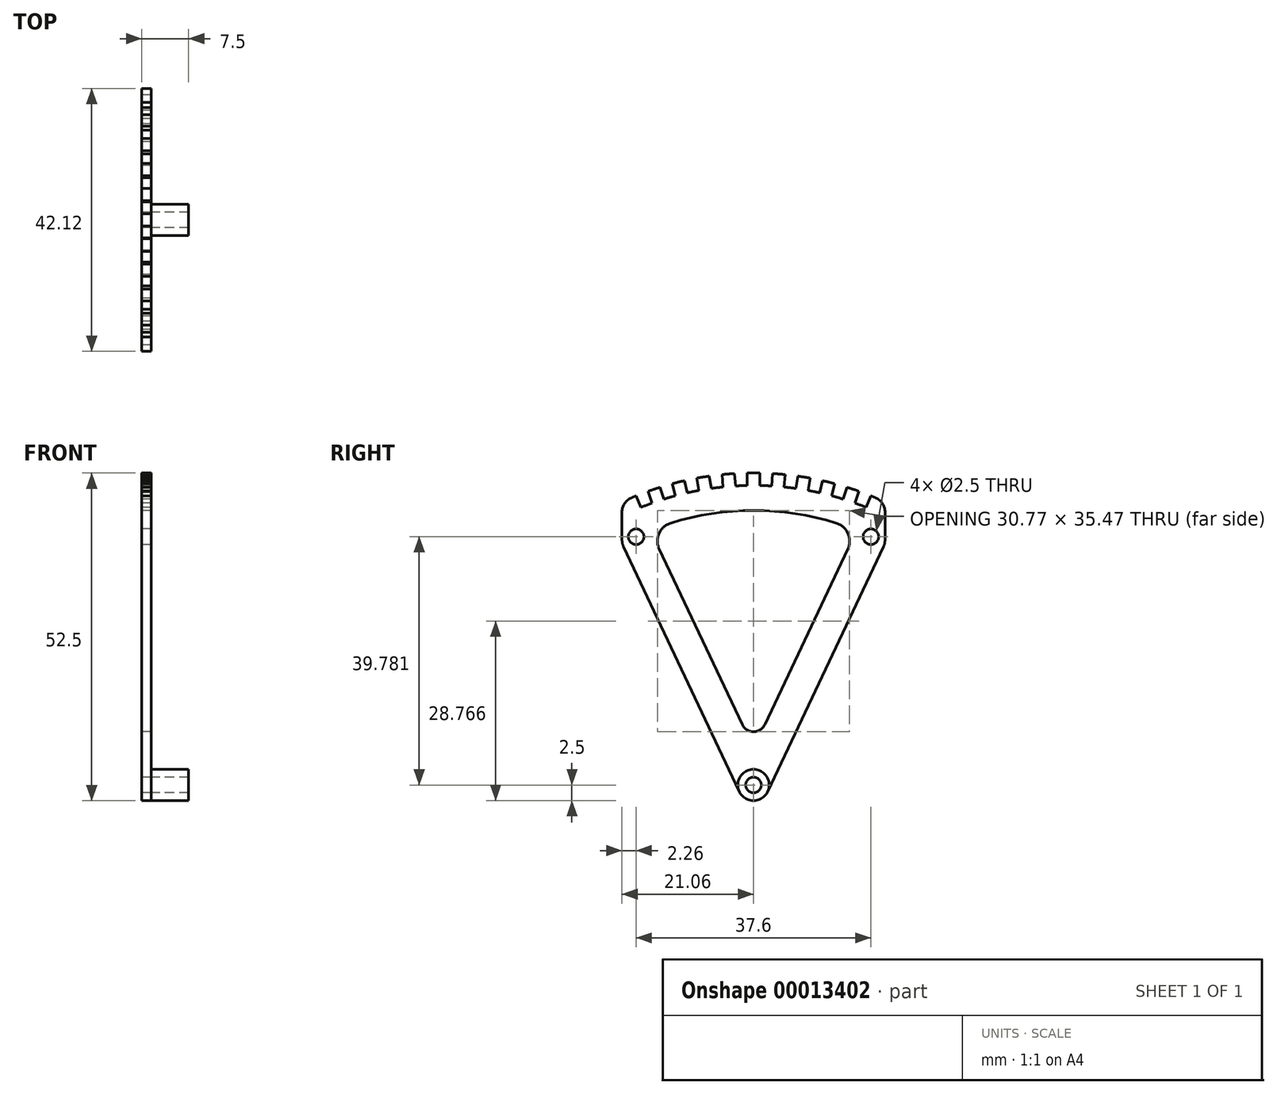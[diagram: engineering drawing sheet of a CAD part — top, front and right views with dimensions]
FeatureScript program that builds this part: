
annotation { "Feature Type Name" : "Feature", "Feature Type Description" : "" }
export const myFeature = defineFeature(function(context is Context, id is Id, definition is map)
    precondition{}
    {
        {
            var Q0;
            Q0=qCreatedBy(makeId("Right.planeOp"),FACE);
            var sketch = newSketch(context, id + "F0", { "sketchPlane" : qUnion([Q0])});
            skCircle(sketch, "E0", {"center": v(0, 0) * mm, "radius": 44 * mm});
            skCircle(sketch, "E1", {"center": v(0, 0) * mm, "radius": 48 * mm});
            skCircle(sketch, "E2", {"center": v(0, 0) * mm, "radius": 50 * mm});
            skLineSegment(sketch, "E3", {"start": v(0, 0) * mm, "end": v(0, 50) * mm, "construction": true});
            skLineSegment(sketch, "E4", {"start": v(-18.8, 39.78) * mm, "end": v(18.8, 39.78) * mm, "construction": true});
            skLineSegment(sketch, "E5", {"start": v(0, 0) * mm, "end": v(-18.8, 39.78) * mm, "construction": true});
            skLineSegment(sketch, "E6.0", {"start": v(2.26, 1.07) * mm, "end": v(-16.54, 40.85) * mm});
            skLineSegment(sketch, "E7.0.MirrorCS", {"start": v(-2.26, -1.07) * mm, "end": v(-21.06, 38.71) * mm});
            skLineSegment(sketch, "E8", {"start": v(-21.06, 38.71) * mm, "end": v(-21.06, 45.35) * mm});
            skPoint(sketch, "E9.orphan", {"position": v(-2.26, -1.07) * mm});
            skLineSegment(sketch, "E10.rect.bottom", {"start": v(-1, 50.26) * mm, "end": v(1, 50.26) * mm});
            skLineSegment(sketch, "E10.rect.top", {"start": v(-1, 45.74) * mm, "end": v(1, 45.74) * mm});
            skLineSegment(sketch, "E10.rect.left", {"start": v(-1, 50.26) * mm, "end": v(-1, 45.74) * mm});
            skLineSegment(sketch, "E10.rect.right", {"start": v(1, 50.26) * mm, "end": v(1, 45.74) * mm});
            skPoint(sketch, "E10.rect.middle", {"position": v(0, 48) * mm});
            skLineSegment(sketch, "E11.1.0", {"start": v(-3.07, 50.18) * mm, "end": v(-2.7, 45.67) * mm});
            skLineSegment(sketch, "E11.1.1", {"start": v(-5.07, 50.01) * mm, "end": v(-4.7, 45.5) * mm});
            skLineSegment(sketch, "E11.1.2", {"start": v(-5.07, 50.01) * mm, "end": v(-3.07, 50.18) * mm});
            skLineSegment(sketch, "E11.2.0", {"start": v(-7.13, 49.76) * mm, "end": v(-6.4, 45.3) * mm});
            skLineSegment(sketch, "E11.2.1", {"start": v(-9.1, 49.44) * mm, "end": v(-8.37, 44.98) * mm});
            skLineSegment(sketch, "E11.2.2", {"start": v(-9.1, 49.44) * mm, "end": v(-7.13, 49.76) * mm});
            skLineSegment(sketch, "E11.3.0", {"start": v(-11.14, 49.02) * mm, "end": v(-10.05, 44.63) * mm});
            skLineSegment(sketch, "E11.3.1", {"start": v(-13.08, 48.54) * mm, "end": v(-11.99, 44.15) * mm});
            skLineSegment(sketch, "E11.3.2", {"start": v(-13.08, 48.54) * mm, "end": v(-11.14, 49.02) * mm});
            skLineSegment(sketch, "E11.4.0", {"start": v(-15.07, 47.96) * mm, "end": v(-13.63, 43.67) * mm});
            skLineSegment(sketch, "E11.4.1", {"start": v(-16.97, 47.32) * mm, "end": v(-15.53, 43.03) * mm});
            skLineSegment(sketch, "E11.4.2", {"start": v(-16.97, 47.32) * mm, "end": v(-15.07, 47.96) * mm});
            skLineSegment(sketch, "E11.5.0", {"start": v(-18.9, 46.58) * mm, "end": v(-17.12, 42.42) * mm});
            skLineSegment(sketch, "E11.5.1", {"start": v(-20.75, 45.8) * mm, "end": v(-18.96, 41.64) * mm});
            skLineSegment(sketch, "E11.5.2", {"start": v(-20.75, 45.8) * mm, "end": v(-18.9, 46.58) * mm});
            skLineSegment(sketch, "E11.anchor1", {"start": v(0, 0) * mm, "end": v(1, 45.74) * mm, "construction": true});
            skLineSegment(sketch, "E11.anchor2", {"start": v(0, 0) * mm, "end": v(-17.12, 42.42) * mm, "construction": true});
            skLineSegment(sketch, "E12.0.MirrorCS", {"start": v(-2.26, 1.07) * mm, "end": v(16.54, 40.85) * mm});
            skLineSegment(sketch, "E13.0.MirrorCS", {"start": v(2.26, -1.07) * mm, "end": v(21.06, 38.71) * mm});
            skLineSegment(sketch, "E14.0.MirrorCS", {"start": v(21.06, 38.71) * mm, "end": v(21.06, 45.35) * mm});
            skLineSegment(sketch, "E15.0.MirrorCS", {"start": v(18.9, 46.58) * mm, "end": v(17.12, 42.42) * mm});
            skLineSegment(sketch, "E16.0.MirrorCS", {"start": v(16.97, 47.32) * mm, "end": v(15.53, 43.03) * mm});
            skLineSegment(sketch, "E17.0.MirrorCS", {"start": v(15.07, 47.96) * mm, "end": v(13.63, 43.67) * mm});
            skLineSegment(sketch, "E18.0.MirrorCS", {"start": v(13.08, 48.54) * mm, "end": v(11.99, 44.15) * mm});
            skLineSegment(sketch, "E19.0.MirrorCS", {"start": v(11.14, 49.02) * mm, "end": v(10.05, 44.63) * mm});
            skLineSegment(sketch, "E20.0.MirrorCS", {"start": v(9.1, 49.44) * mm, "end": v(8.37, 44.98) * mm});
            skLineSegment(sketch, "E21.0.MirrorCS", {"start": v(7.13, 49.76) * mm, "end": v(6.4, 45.3) * mm});
            skLineSegment(sketch, "E22.0.MirrorCS", {"start": v(5.07, 50.01) * mm, "end": v(4.7, 45.5) * mm});
            skLineSegment(sketch, "E23.0.MirrorCS", {"start": v(3.07, 50.18) * mm, "end": v(2.7, 45.67) * mm});
            skCircle(sketch, "E24", {"center": v(-18.8, 39.78) * mm, "radius": 1.25 * mm});
            skCircle(sketch, "E25", {"center": v(0, 0) * mm, "radius": 1.25 * mm});
            skCircle(sketch, "E26.0.MirrorC", {"center": v(18.8, 39.78) * mm, "radius": 1.25 * mm});
            skPoint(sketch, "E27.visualSharp", {"position": v(0, -5.85) * mm});
            skArc(sketch, "E27.filletArc", {"start": v(-2.26, -1.07) * mm, "mid": v(0, -2.5) * mm, "end": v(2.26, -1.07) * mm});
            skSolve(sketch);
        }
        {
            var Q0;
            Q0=makeQuery(id+"F0.imprint","IMPRINT",FACE,{"disambiguationData":[TD([[makeQuery(id+"F0.imprint","IMPRINT",EDGE,{"derivedFrom":sQuery(id+"F0.wireOp",EDGE,"E25")}),-1.0]])]});
            var Q1;
            {var subQ63=sQuery(id+"F0.wireOp",EDGE,"E10.rect.top");Q1=makeQuery(id+"F0.imprint","IMPRINT",FACE,{"disambiguationData":[TD([[makeQuery(id+"F0.imprint","IMPRINT",EDGE,{"derivedFrom":subQ63}),-1.0]])]});}
            var Q2;
            {var subQ3=sQuery(id+"F0.wireOp",EDGE,"E10.rect.top");Q2=makeQuery(id+"F0.imprint","IMPRINT",FACE,{"disambiguationData":[TD([[makeQuery(id+"F0.imprint","IMPRINT",EDGE,{"derivedFrom":subQ3}),1.0]])]});}
            var Q3;
            {var subQ0=sQuery(id+"F0.wireOp",EDGE,"E11.5.1");var subQ3=sQuery(id+"F0.wireOp",EDGE,"E1");var subQ4=makeQuery(id+"F0.imprint","INTERSECT",VERTEX,{"derivedFrom":[subQ3,subQ0]});Q3=makeQuery(id+"F0.imprint","IMPRINT",FACE,{"disambiguationData":[TD([[makeQuery(id+"F0.imprint","IMPRINT",EDGE,{"disambiguationData":[TD([[subQ4,-1.0]])],"derivedFrom":subQ3}),-1.0]])]});}
            var Q4;
            {var subQ3=sQuery(id+"F0.wireOp",EDGE,"E11.5.0");var subQ5=sQuery(id+"F0.wireOp",EDGE,"E1");var subQ7=makeQuery(id+"F0.imprint","INTERSECT",VERTEX,{"derivedFrom":[subQ5,subQ3]});Q4=makeQuery(id+"F0.imprint","IMPRINT",FACE,{"disambiguationData":[TD([[makeQuery(id+"F0.imprint","IMPRINT",EDGE,{"disambiguationData":[TD([[subQ7,-1.0]])],"derivedFrom":subQ5}),-1.0]])]});}
            var Q5;
            {var subQ3=sQuery(id+"F0.wireOp",EDGE,"E11.4.0");var subQ5=sQuery(id+"F0.wireOp",EDGE,"E1");var subQ7=makeQuery(id+"F0.imprint","INTERSECT",VERTEX,{"derivedFrom":[subQ5,subQ3]});Q5=makeQuery(id+"F0.imprint","IMPRINT",FACE,{"disambiguationData":[TD([[makeQuery(id+"F0.imprint","IMPRINT",EDGE,{"disambiguationData":[TD([[subQ7,-1.0]])],"derivedFrom":subQ5}),-1.0]])]});}
            var Q6;
            {var subQ3=sQuery(id+"F0.wireOp",EDGE,"E11.3.0");var subQ5=sQuery(id+"F0.wireOp",EDGE,"E1");var subQ7=makeQuery(id+"F0.imprint","INTERSECT",VERTEX,{"derivedFrom":[subQ5,subQ3]});Q6=makeQuery(id+"F0.imprint","IMPRINT",FACE,{"disambiguationData":[TD([[makeQuery(id+"F0.imprint","IMPRINT",EDGE,{"disambiguationData":[TD([[subQ7,-1.0]])],"derivedFrom":subQ5}),-1.0]])]});}
            var Q7;
            {var subQ3=sQuery(id+"F0.wireOp",EDGE,"E11.2.0");var subQ5=sQuery(id+"F0.wireOp",EDGE,"E1");var subQ7=makeQuery(id+"F0.imprint","INTERSECT",VERTEX,{"derivedFrom":[subQ5,subQ3]});Q7=makeQuery(id+"F0.imprint","IMPRINT",FACE,{"disambiguationData":[TD([[makeQuery(id+"F0.imprint","IMPRINT",EDGE,{"disambiguationData":[TD([[subQ7,-1.0]])],"derivedFrom":subQ5}),-1.0]])]});}
            var Q8;
            {var subQ3=sQuery(id+"F0.wireOp",EDGE,"E11.1.0");var subQ5=sQuery(id+"F0.wireOp",EDGE,"E1");var subQ7=makeQuery(id+"F0.imprint","INTERSECT",VERTEX,{"derivedFrom":[subQ5,subQ3]});Q8=makeQuery(id+"F0.imprint","IMPRINT",FACE,{"disambiguationData":[TD([[makeQuery(id+"F0.imprint","IMPRINT",EDGE,{"disambiguationData":[TD([[subQ7,-1.0]])],"derivedFrom":subQ5}),-1.0]])]});}
            var Q9;
            {var subQ1=sQuery(id+"F0.wireOp",EDGE,"E10.rect.right");var subQ5=sQuery(id+"F0.wireOp",EDGE,"E1");var subQ6=makeQuery(id+"F0.imprint","INTERSECT",VERTEX,{"derivedFrom":[subQ5,subQ1]});Q9=makeQuery(id+"F0.imprint","IMPRINT",FACE,{"disambiguationData":[TD([[makeQuery(id+"F0.imprint","IMPRINT",EDGE,{"disambiguationData":[TD([[subQ6,-1.0]])],"derivedFrom":subQ5}),-1.0]])]});}
            var Q10;
            {var subQ1=sQuery(id+"F0.wireOp",EDGE,"E1");var subQ5=sQuery(id+"F0.wireOp",EDGE,"E22.0.MirrorCS");var subQ6=makeQuery(id+"F0.imprint","INTERSECT",VERTEX,{"derivedFrom":[subQ1,subQ5]});Q10=makeQuery(id+"F0.imprint","IMPRINT",FACE,{"disambiguationData":[TD([[makeQuery(id+"F0.imprint","IMPRINT",EDGE,{"disambiguationData":[TD([[subQ6,-1.0]])],"derivedFrom":subQ1}),-1.0]])]});}
            var Q11;
            {var subQ1=sQuery(id+"F0.wireOp",EDGE,"E1");var subQ5=sQuery(id+"F0.wireOp",EDGE,"E20.0.MirrorCS");var subQ7=makeQuery(id+"F0.imprint","INTERSECT",VERTEX,{"derivedFrom":[subQ1,subQ5]});Q11=makeQuery(id+"F0.imprint","IMPRINT",FACE,{"disambiguationData":[TD([[makeQuery(id+"F0.imprint","IMPRINT",EDGE,{"disambiguationData":[TD([[subQ7,-1.0]])],"derivedFrom":subQ1}),-1.0]])]});}
            var Q12;
            {var subQ0=sQuery(id+"F0.wireOp",EDGE,"E18.0.MirrorCS");var subQ1=sQuery(id+"F0.wireOp",EDGE,"E1");var subQ2=makeQuery(id+"F0.imprint","INTERSECT",VERTEX,{"derivedFrom":[subQ1,subQ0]});Q12=makeQuery(id+"F0.imprint","IMPRINT",FACE,{"disambiguationData":[TD([[makeQuery(id+"F0.imprint","IMPRINT",EDGE,{"disambiguationData":[TD([[subQ2,-1.0]])],"derivedFrom":subQ1}),-1.0]])]});}
            var Q13;
            {var subQ1=sQuery(id+"F0.wireOp",EDGE,"E1");var subQ5=sQuery(id+"F0.wireOp",EDGE,"E16.0.MirrorCS");var subQ6=makeQuery(id+"F0.imprint","INTERSECT",VERTEX,{"derivedFrom":[subQ1,subQ5]});Q13=makeQuery(id+"F0.imprint","IMPRINT",FACE,{"disambiguationData":[TD([[makeQuery(id+"F0.imprint","IMPRINT",EDGE,{"disambiguationData":[TD([[subQ6,-1.0]])],"derivedFrom":subQ1}),-1.0]])]});}
            var Q14;
            {var subQ0=sQuery(id+"F0.wireOp",EDGE,"E15.0.MirrorCS");var subQ1=sQuery(id+"F0.wireOp",EDGE,"E1");var subQ2=makeQuery(id+"F0.imprint","INTERSECT",VERTEX,{"derivedFrom":[subQ1,subQ0]});Q14=makeQuery(id+"F0.imprint","IMPRINT",FACE,{"disambiguationData":[TD([[makeQuery(id+"F0.imprint","IMPRINT",EDGE,{"disambiguationData":[TD([[subQ2,1.0]])],"derivedFrom":subQ1}),-1.0]])]});}
            extrude(context, id + "F1", {"entities" : qUnion([Q0, Q1, Q2, Q3, Q4, Q5, Q6, Q7, Q8, Q9, Q10, Q11, Q12, Q13, Q14]), "depth" : 1.5 * mm});
        }
        {
            var Q0;
            Q0=makeQuery(id+"F1.opExtrude","SWEPT_EDGE",EDGE,{"disambiguationData":[OSD([sQuery(id+"F0.wireOp",EDGE,"E6.0"),sQuery(id+"F0.wireOp",EDGE,"E12.0.MirrorCS")])]});
            fillet(context, id + "F2", {"entities" : qUnion([Q0]), "radius" : 2 * mm, "tangentPropagation" : true, "allowEdgeOverflow" : false});
        }
        {
            var Q0;
            Q0=makeQuery(id+"F1.opExtrude","SWEPT_EDGE",EDGE,{"disambiguationData":[OSD([sQuery(id+"F0.wireOp",EDGE,"E0"),sQuery(id+"F0.wireOp",EDGE,"E6.0")])]});
            var Q1;
            Q1=makeQuery(id+"F1.opExtrude","SWEPT_EDGE",EDGE,{"disambiguationData":[OSD([sQuery(id+"F0.wireOp",EDGE,"E0"),sQuery(id+"F0.wireOp",EDGE,"E12.0.MirrorCS")])]});
            fillet(context, id + "F3", {"entities" : qUnion([Q0, Q1]), "radius" : 3 * mm, "tangentPropagation" : true, "allowEdgeOverflow" : false});
        }
        {
            var Q0;
            Q0=makeQuery(id+"F1.opExtrude","SWEPT_EDGE",EDGE,{"disambiguationData":[OSD([sQuery(id+"F0.wireOp",EDGE,"E7.0.MirrorCS"),sQuery(id+"F0.wireOp",EDGE,"E8")])]});
            var Q1;
            Q1=makeQuery(id+"F1.opExtrude","SWEPT_EDGE",EDGE,{"disambiguationData":[OSD([sQuery(id+"F0.wireOp",EDGE,"E13.0.MirrorCS"),sQuery(id+"F0.wireOp",EDGE,"E14.0.MirrorCS")])]});
            var Q2;
            Q2=makeQuery(id+"F1.opExtrude","SWEPT_EDGE",EDGE,{"disambiguationData":[OSD([sQuery(id+"F0.wireOp",EDGE,"E14.0.MirrorCS"),sQuery(id+"F0.wireOp",EDGE,"E2")])]});
            var Q3;
            Q3=makeQuery(id+"F1.opExtrude","SWEPT_EDGE",EDGE,{"disambiguationData":[OSD([sQuery(id+"F0.wireOp",EDGE,"E8"),sQuery(id+"F0.wireOp",EDGE,"E2")])]});
            fillet(context, id + "F4", {"entities" : qUnion([Q0, Q1, Q2, Q3]), "radius" : 2.5 * mm, "tangentPropagation" : true, "allowEdgeOverflow" : false});
        }
        {
            var Q0;
            Q0=makeQuery(id+"F1.opExtrude","CAP_FACE",FACE,{"disambiguationData":[OSD([sQuery(id+"F0.wireOp",EDGE,"E0"),sQuery(id+"F0.wireOp",EDGE,"E1"),sQuery(id+"F0.wireOp",EDGE,"E6.0"),sQuery(id+"F0.wireOp",EDGE,"E7.0.MirrorCS"),sQuery(id+"F0.wireOp",EDGE,"E8"),sQuery(id+"F0.wireOp",EDGE,"E10.rect.left"),sQuery(id+"F0.wireOp",EDGE,"E10.rect.right"),sQuery(id+"F0.wireOp",EDGE,"E11.1.0"),sQuery(id+"F0.wireOp",EDGE,"E11.1.1"),sQuery(id+"F0.wireOp",EDGE,"E11.2.0"),sQuery(id+"F0.wireOp",EDGE,"E11.2.1"),sQuery(id+"F0.wireOp",EDGE,"E11.3.0"),sQuery(id+"F0.wireOp",EDGE,"E11.3.1"),sQuery(id+"F0.wireOp",EDGE,"E11.4.0"),sQuery(id+"F0.wireOp",EDGE,"E11.4.1"),sQuery(id+"F0.wireOp",EDGE,"E11.5.0"),sQuery(id+"F0.wireOp",EDGE,"E12.0.MirrorCS"),sQuery(id+"F0.wireOp",EDGE,"E13.0.MirrorCS"),sQuery(id+"F0.wireOp",EDGE,"E14.0.MirrorCS"),sQuery(id+"F0.wireOp",EDGE,"E2"),sQuery(id+"F0.wireOp",EDGE,"E15.0.MirrorCS"),sQuery(id+"F0.wireOp",EDGE,"E16.0.MirrorCS"),sQuery(id+"F0.wireOp",EDGE,"E17.0.MirrorCS"),sQuery(id+"F0.wireOp",EDGE,"E18.0.MirrorCS"),sQuery(id+"F0.wireOp",EDGE,"E19.0.MirrorCS"),sQuery(id+"F0.wireOp",EDGE,"E20.0.MirrorCS"),sQuery(id+"F0.wireOp",EDGE,"E21.0.MirrorCS"),sQuery(id+"F0.wireOp",EDGE,"E22.0.MirrorCS"),sQuery(id+"F0.wireOp",EDGE,"E23.0.MirrorCS"),sQuery(id+"F0.wireOp",EDGE,"E24"),sQuery(id+"F0.wireOp",EDGE,"E25"),sQuery(id+"F0.wireOp",EDGE,"E26.0.MirrorC"),sQuery(id+"F0.wireOp",EDGE,"E27.filletArc")])],"isStart":false});
            var sketch = newSketch(context, id + "F5", { "sketchPlane" : qUnion([Q0])});
            skCircle(sketch, "E28", {"center": v(0, 0) * mm, "radius": 2.5 * mm});
            skSolve(sketch);
        }
        {
            var Q0;
            Q0=makeQuery(id+"F5.imprint","IMPRINT",FACE,{"disambiguationData":[TD([[makeQuery(id+"F5.imprint","IMPRINT",EDGE,{"derivedFrom":makeQuery(id+"F1.opExtrude","CAP_EDGE",EDGE,{"disambiguationData":[OSD([sQuery(id+"F0.wireOp",EDGE,"E25")])],"isStart":false})}),-1.0]])]});
            extrude(context, id + "F6", {"entities" : qUnion([Q0]), "depth" : 6 * mm});
        }
    });
